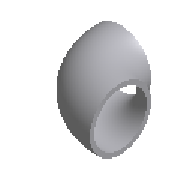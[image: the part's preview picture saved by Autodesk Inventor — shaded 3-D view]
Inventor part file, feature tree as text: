
AUTODESK INVENTOR PART (.ipt)
format: ipt  version: 2023.2 (Build 272271030, 271C)  size: 189,440 bytes
history: native  units: mm (DEFAULTED — no unit token found)
features: other x4, sketch x2, sweep x1
ambient origin geometry x8: Origin, YZ Plane, XZ Plane, XY Plane, X Axis, Y Axis, Z Axis, Center Point
bodies: Solid1 (feature_tree)
feature tree (7):
  sweep  "Sweep1"
  other  "Work Point1"
  other  "Work Point2"
  other  "Work Axis1"
  other  "Work Axis2"
  sketch  "Sketch1"  dims[d0=109.1mm d1=114.3mm]
  sketch  "Sketch2"  dims[d2=102.0mm d3=102.0mm d4=0.0mm d5=0.0mm]
